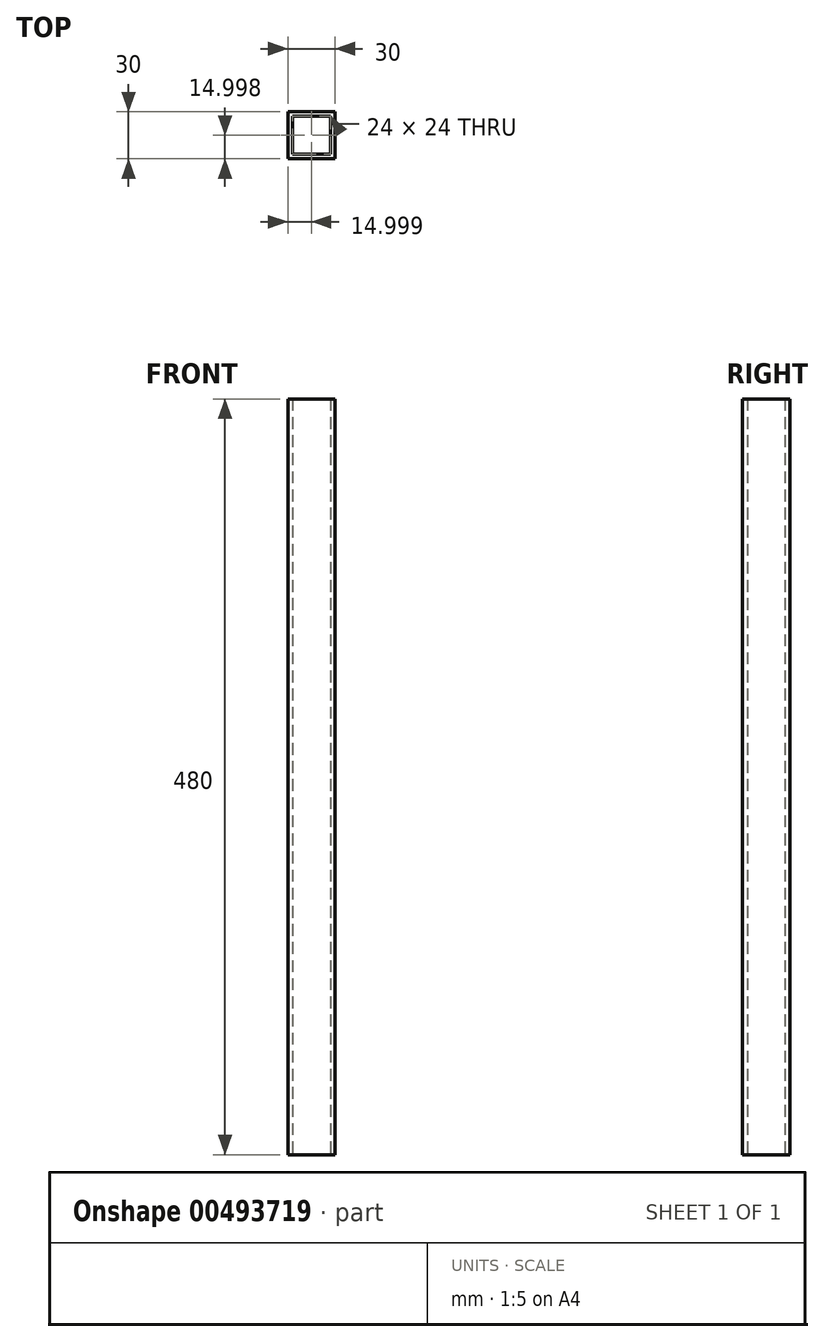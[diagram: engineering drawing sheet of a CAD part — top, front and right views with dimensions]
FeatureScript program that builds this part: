
annotation { "Feature Type Name" : "Feature", "Feature Type Description" : "" }
export const myFeature = defineFeature(function(context is Context, id is Id, definition is map)
    precondition{}
    {
        {
            var Q0;
            Q0=qCreatedBy(makeId("Top.planeOp"),FACE);
            var sketch = newSketch(context, id + "F0", { "sketchPlane" : qUnion([Q0])});
            skLineSegment(sketch, "E0.bottom", {"start": v(-21, 16.5) * mm, "end": v(9, 16.5) * mm});
            skLineSegment(sketch, "E0.top", {"start": v(-21, -13.5) * mm, "end": v(9, -13.5) * mm});
            skLineSegment(sketch, "E0.left", {"start": v(-21, 16.5) * mm, "end": v(-21, -13.5) * mm});
            skLineSegment(sketch, "E0.right", {"start": v(9, 16.5) * mm, "end": v(9, -13.5) * mm});
            skLineSegment(sketch, "E1.bottom", {"start": v(-18, 13.5) * mm, "end": v(6, 13.5) * mm});
            skLineSegment(sketch, "E1.top", {"start": v(-18, -10.5) * mm, "end": v(6, -10.5) * mm});
            skLineSegment(sketch, "E1.left", {"start": v(-18, 13.5) * mm, "end": v(-18, -10.5) * mm});
            skLineSegment(sketch, "E1.right", {"start": v(6, 13.5) * mm, "end": v(6, -10.5) * mm});
            skSolve(sketch);
        }
        {
            var Q0;
            Q0 = qSketchRegion(id + "F0", true);
            extrude(context, id + "F1", {"entities" : qUnion([Q0]), "depth" : 480 * mm});
        }
    });
